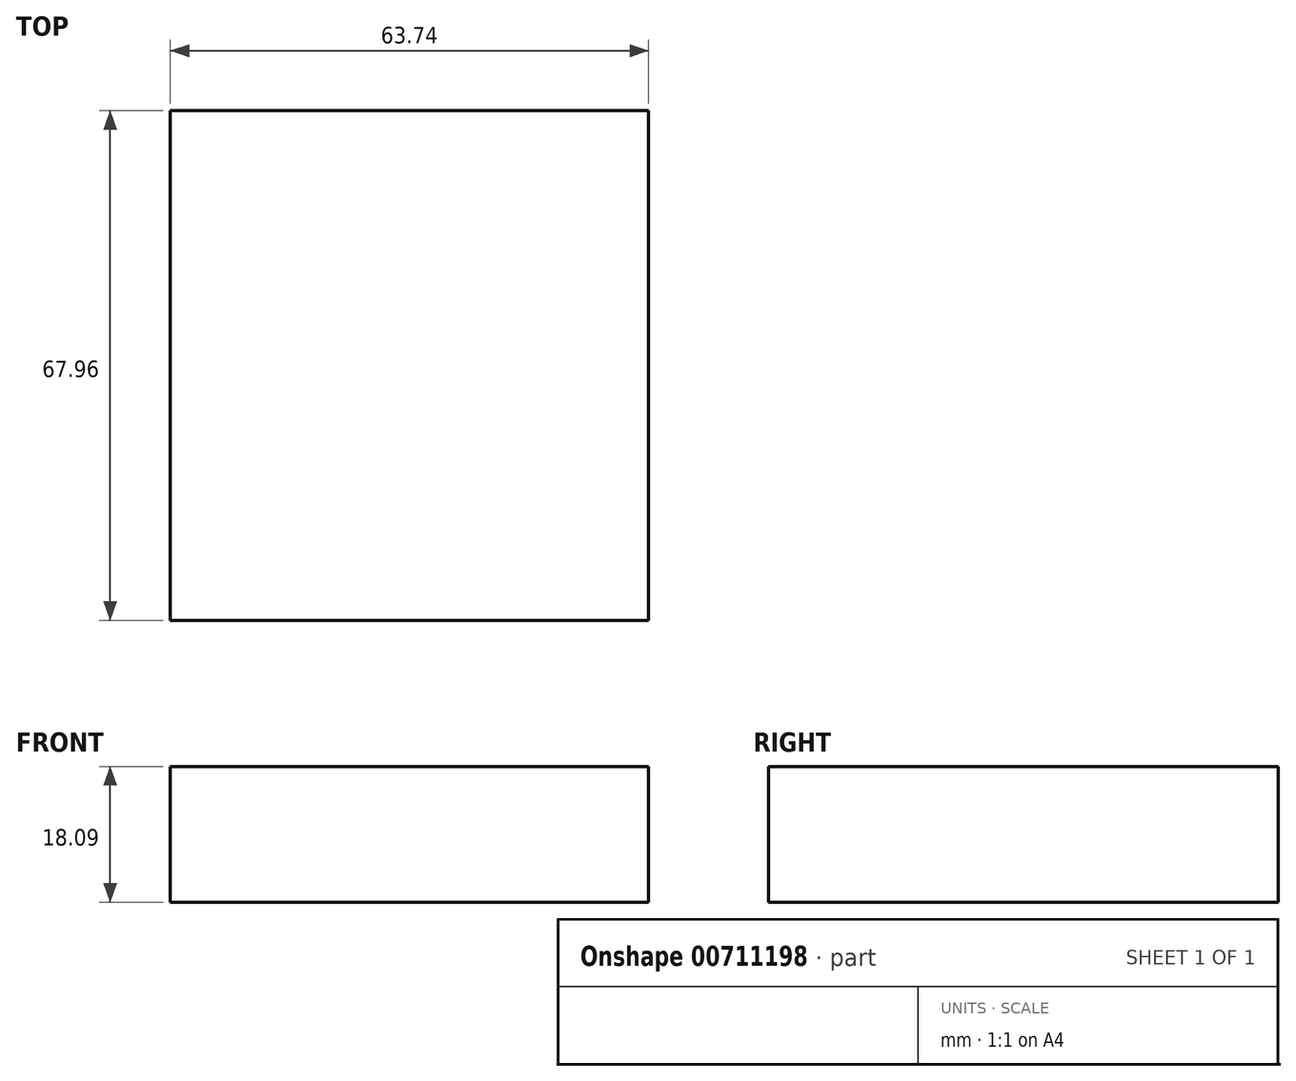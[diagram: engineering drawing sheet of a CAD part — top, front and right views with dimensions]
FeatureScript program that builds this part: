
annotation { "Feature Type Name" : "Feature", "Feature Type Description" : "" }
export const myFeature = defineFeature(function(context is Context, id is Id, definition is map)
    precondition{}
    {
        {
            var Q0;
            Q0=qCreatedBy(makeId("Top.planeOp"),FACE);
            var sketch = newSketch(context, id + "F0", { "sketchPlane" : qUnion([Q0])});
            skLineSegment(sketch, "E0.bottom", {"start": v(-34.69, 40.9) * mm, "end": v(29.05, 40.9) * mm});
            skLineSegment(sketch, "E0.top", {"start": v(-34.69, -27.07) * mm, "end": v(29.05, -27.07) * mm});
            skLineSegment(sketch, "E0.left", {"start": v(-34.69, 40.9) * mm, "end": v(-34.69, -27.07) * mm});
            skLineSegment(sketch, "E0.right", {"start": v(29.05, 40.9) * mm, "end": v(29.05, -27.07) * mm});
            skSolve(sketch);
        }
        {
            var Q0;
            Q0=makeQuery(id+"F0.imprint","IMPRINT",FACE,{"disambiguationData":[TD([[makeQuery(id+"F0.imprint","IMPRINT",EDGE,{"derivedFrom":sQuery(id+"F0.wireOp",EDGE,"E0.bottom")}),-1.0]])]});
            var sketch = newSketch(context, id + "F1", { "sketchPlane" : qUnion([Q0])});
            skSolve(sketch);
        }
        {
            var Q0;
            Q0=makeQuery(id+"F1.imprint","IMPRINT",FACE,{"disambiguationData":[TD([[makeQuery(id+"F1.imprint","IMPRINT",EDGE,{"derivedFrom":makeQuery(id+"F0.imprint","IMPRINT",EDGE,{"derivedFrom":sQuery(id+"F0.wireOp",EDGE,"E0.bottom")})}),-1.0]])]});
            extrude(context, id + "F2", {"entities" : qUnion([Q0]), "depth" : 18.09 * mm, "offsetDistance" : 25.4 * mm});
        }
    });
